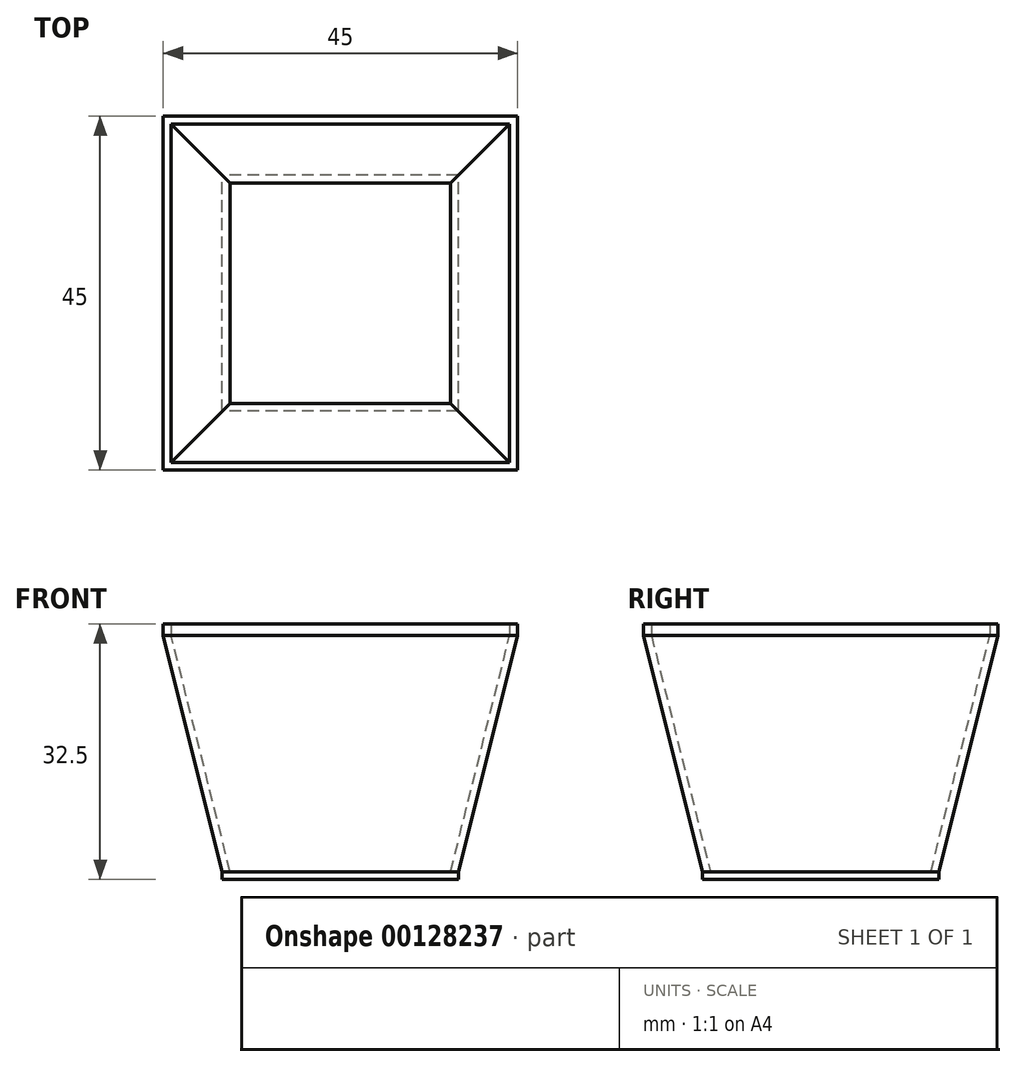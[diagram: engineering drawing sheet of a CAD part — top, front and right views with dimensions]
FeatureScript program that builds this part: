
annotation { "Feature Type Name" : "Feature", "Feature Type Description" : "" }
export const myFeature = defineFeature(function(context is Context, id is Id, definition is map)
    precondition{}
    {
        {
            var Q0;
            Q0=qCreatedBy(makeId("Top.planeOp"),FACE);
            var sketch = newSketch(context, id + "F0", { "sketchPlane" : qUnion([Q0])});
            skLineSegment(sketch, "E0.bottom", {"start": v(14, -14) * mm, "end": v(-14, -14) * mm});
            skLineSegment(sketch, "E0.top", {"start": v(14, 14) * mm, "end": v(-14, 14) * mm});
            skLineSegment(sketch, "E0.left", {"start": v(14, -14) * mm, "end": v(14, 14) * mm});
            skLineSegment(sketch, "E0.right", {"start": v(-14, -14) * mm, "end": v(-14, 14) * mm});
            skPoint(sketch, "E0.middle", {"position": v(0, 0) * mm});
            skLineSegment(sketch, "E1.0", {"start": v(15, 15) * mm, "end": v(-15, 15) * mm});
            skLineSegment(sketch, "E1.1", {"start": v(15, -15) * mm, "end": v(15, 15) * mm});
            skLineSegment(sketch, "E1.2", {"start": v(15, -15) * mm, "end": v(-15, -15) * mm});
            skLineSegment(sketch, "E1.3", {"start": v(-15, -15) * mm, "end": v(-15, 15) * mm});
            skLineSegment(sketch, "E2", {"start": v(-14, -14) * mm, "end": v(-15, -15) * mm});
            skLineSegment(sketch, "E3", {"start": v(-15, 15) * mm, "end": v(-14, 14) * mm});
            skLineSegment(sketch, "E4", {"start": v(14, 14) * mm, "end": v(15, 15) * mm});
            skLineSegment(sketch, "E5", {"start": v(14, -14) * mm, "end": v(15, -15) * mm});
            skSolve(sketch);
        }
        {
            var Q0;
            Q0=makeQuery(id+"F0.imprint","IMPRINT",FACE,{"disambiguationData":[TD([[makeQuery(id+"F0.imprint","IMPRINT",EDGE,{"derivedFrom":sQuery(id+"F0.wireOp",EDGE,"E0.bottom")}),-1.0]])]});
            cPlane(context, id + "F1", {"entities" : qUnion([Q0]), "cplaneType" : CPlaneType.OFFSET, "offset" : 30 * mm, "width" : 150 * mm, "height" : 150 * mm});
        }
        {
            var Q0;
            Q0=qCreatedBy(id+"F1.planeOp",FACE);
            var sketch = newSketch(context, id + "F2", { "sketchPlane" : qUnion([Q0])});
            skLineSegment(sketch, "E6.bottom", {"start": v(21.5, -21.5) * mm, "end": v(-21.5, -21.5) * mm});
            skLineSegment(sketch, "E6.top", {"start": v(21.5, 21.5) * mm, "end": v(-21.5, 21.5) * mm});
            skLineSegment(sketch, "E6.left", {"start": v(21.5, -21.5) * mm, "end": v(21.5, 21.5) * mm});
            skLineSegment(sketch, "E6.right", {"start": v(-21.5, -21.5) * mm, "end": v(-21.5, 21.5) * mm});
            skPoint(sketch, "E6.middle", {"position": v(0, 0) * mm});
            skLineSegment(sketch, "E7.0", {"start": v(22.5, 22.5) * mm, "end": v(-22.5, 22.5) * mm});
            skLineSegment(sketch, "E7.1", {"start": v(22.5, -22.5) * mm, "end": v(22.5, 22.5) * mm});
            skLineSegment(sketch, "E7.2", {"start": v(22.5, -22.5) * mm, "end": v(-22.5, -22.5) * mm});
            skLineSegment(sketch, "E7.3", {"start": v(-22.5, -22.5) * mm, "end": v(-22.5, 22.5) * mm});
            skLineSegment(sketch, "E8", {"start": v(21.5, 21.5) * mm, "end": v(22.5, 22.5) * mm});
            skLineSegment(sketch, "E9", {"start": v(22.5, -22.5) * mm, "end": v(21.5, -21.5) * mm});
            skLineSegment(sketch, "E10", {"start": v(-21.5, -21.5) * mm, "end": v(-22.5, -22.5) * mm});
            skLineSegment(sketch, "E11", {"start": v(-22.5, 22.5) * mm, "end": v(-21.5, 21.5) * mm});
            skLineSegment(sketch, "E12.0.0", {"start": v(-14, -14) * mm, "end": v(14, -14) * mm, "construction": true});
            skLineSegment(sketch, "E12.0.1", {"start": v(14, -14) * mm, "end": v(14, 14) * mm, "construction": true});
            skLineSegment(sketch, "E12.0.2", {"start": v(14, 14) * mm, "end": v(-14, 14) * mm, "construction": true});
            skLineSegment(sketch, "E12.0.3", {"start": v(-14, 14) * mm, "end": v(-14, -14) * mm, "construction": true});
            skSolve(sketch);
        }
        {
            var Q0;
            Q0=makeQuery(id+"F2.imprint","IMPRINT",FACE,{"disambiguationData":[TD([[makeQuery(id+"F2.imprint","IMPRINT",EDGE,{"derivedFrom":sQuery(id+"F2.wireOp",EDGE,"E6.bottom")}),1.0]])]});
            var Q1;
            Q1=makeQuery(id+"F0.imprint","IMPRINT",FACE,{"disambiguationData":[TD([[makeQuery(id+"F0.imprint","IMPRINT",EDGE,{"derivedFrom":sQuery(id+"F0.wireOp",EDGE,"E0.bottom")}),1.0]])]});
            loft(context, id + "F3", {"sheetProfilesArray" : [{ "sheetProfileEntities" : qUnion([Q0]) }, { "sheetProfileEntities" : qUnion([Q1]) }]});
        }
        {
            var Q1;
            Q1=makeQuery(id+"F0.imprint","IMPRINT",FACE,{"disambiguationData":[TD([[makeQuery(id+"F0.imprint","IMPRINT",EDGE,{"derivedFrom":sQuery(id+"F0.wireOp",EDGE,"E0.left")}),-1.0]])]});
            var Q2;
            Q2=makeQuery(id+"F2.imprint","IMPRINT",FACE,{"disambiguationData":[TD([[makeQuery(id+"F2.imprint","IMPRINT",EDGE,{"derivedFrom":sQuery(id+"F2.wireOp",EDGE,"E6.left")}),-1.0]])]});
            loft(context, id + "F4", {"operationType" : NewBodyOperationType.ADD, "sheetProfilesArray" : [{ "sheetProfileEntities" : qUnion([Q1]) }, { "sheetProfileEntities" : qUnion([Q2]) }]});
        }
        {
            var Q1;
            Q1=makeQuery(id+"F0.imprint","IMPRINT",FACE,{"disambiguationData":[TD([[makeQuery(id+"F0.imprint","IMPRINT",EDGE,{"derivedFrom":sQuery(id+"F0.wireOp",EDGE,"E0.top")}),-1.0]])]});
            var Q2;
            Q2=makeQuery(id+"F2.imprint","IMPRINT",FACE,{"disambiguationData":[TD([[makeQuery(id+"F2.imprint","IMPRINT",EDGE,{"derivedFrom":sQuery(id+"F2.wireOp",EDGE,"E6.top")}),-1.0]])]});
            loft(context, id + "F5", {"operationType" : NewBodyOperationType.ADD, "sheetProfilesArray" : [{ "sheetProfileEntities" : qUnion([Q1]) }, { "sheetProfileEntities" : qUnion([Q2]) }]});
        }
        {
            var Q1;
            Q1=makeQuery(id+"F0.imprint","IMPRINT",FACE,{"disambiguationData":[TD([[makeQuery(id+"F0.imprint","IMPRINT",EDGE,{"derivedFrom":sQuery(id+"F0.wireOp",EDGE,"E0.right")}),1.0]])]});
            var Q2;
            Q2=makeQuery(id+"F2.imprint","IMPRINT",FACE,{"disambiguationData":[TD([[makeQuery(id+"F2.imprint","IMPRINT",EDGE,{"derivedFrom":sQuery(id+"F2.wireOp",EDGE,"E6.right")}),1.0]])]});
            loft(context, id + "F6", {"operationType" : NewBodyOperationType.ADD, "sheetProfilesArray" : [{ "sheetProfileEntities" : qUnion([Q1]) }, { "sheetProfileEntities" : qUnion([Q2]) }]});
        }
        {
            var Q0;
            Q0=makeQuery(id+"F0.imprint","IMPRINT",FACE,{"disambiguationData":[TD([[makeQuery(id+"F0.imprint","IMPRINT",EDGE,{"derivedFrom":sQuery(id+"F0.wireOp",EDGE,"E0.top")}),-1.0]])]});
            var Q1;
            Q1=makeQuery(id+"F0.imprint","IMPRINT",FACE,{"disambiguationData":[TD([[makeQuery(id+"F0.imprint","IMPRINT",EDGE,{"derivedFrom":sQuery(id+"F0.wireOp",EDGE,"E0.right")}),1.0]])]});
            var Q2;
            Q2=makeQuery(id+"F0.imprint","IMPRINT",FACE,{"disambiguationData":[TD([[makeQuery(id+"F0.imprint","IMPRINT",EDGE,{"derivedFrom":sQuery(id+"F0.wireOp",EDGE,"E0.bottom")}),1.0]])]});
            var Q3;
            Q3=makeQuery(id+"F0.imprint","IMPRINT",FACE,{"disambiguationData":[TD([[makeQuery(id+"F0.imprint","IMPRINT",EDGE,{"derivedFrom":sQuery(id+"F0.wireOp",EDGE,"E0.left")}),-1.0]])]});
            var Q4;
            Q4=makeQuery(id+"F0.imprint","IMPRINT",FACE,{"disambiguationData":[TD([[makeQuery(id+"F0.imprint","IMPRINT",EDGE,{"derivedFrom":sQuery(id+"F0.wireOp",EDGE,"E0.bottom")}),-1.0]])]});
            extrude(context, id + "F7", {"entities" : qUnion([Q0, Q1, Q2, Q3, Q4]), "operationType" : NewBodyOperationType.ADD, "oppositeDirection" : true, "depth" : 1 * mm});
        }
        {
            var Q0;
            Q0=makeQuery(id+"F2.imprint","IMPRINT",FACE,{"disambiguationData":[TD([[makeQuery(id+"F2.imprint","IMPRINT",EDGE,{"derivedFrom":sQuery(id+"F2.wireOp",EDGE,"E6.bottom")}),1.0]])]});
            var Q1;
            Q1=makeQuery(id+"F2.imprint","IMPRINT",FACE,{"disambiguationData":[TD([[makeQuery(id+"F2.imprint","IMPRINT",EDGE,{"derivedFrom":sQuery(id+"F2.wireOp",EDGE,"E6.left")}),-1.0]])]});
            var Q2;
            Q2=makeQuery(id+"F2.imprint","IMPRINT",FACE,{"disambiguationData":[TD([[makeQuery(id+"F2.imprint","IMPRINT",EDGE,{"derivedFrom":sQuery(id+"F2.wireOp",EDGE,"E6.top")}),-1.0]])]});
            var Q3;
            Q3=makeQuery(id+"F2.imprint","IMPRINT",FACE,{"disambiguationData":[TD([[makeQuery(id+"F2.imprint","IMPRINT",EDGE,{"derivedFrom":sQuery(id+"F2.wireOp",EDGE,"E6.right")}),1.0]])]});
            extrude(context, id + "F8", {"entities" : qUnion([Q0, Q1, Q2, Q3]), "operationType" : NewBodyOperationType.ADD, "depth" : 1.5 * mm});
        }
    });
